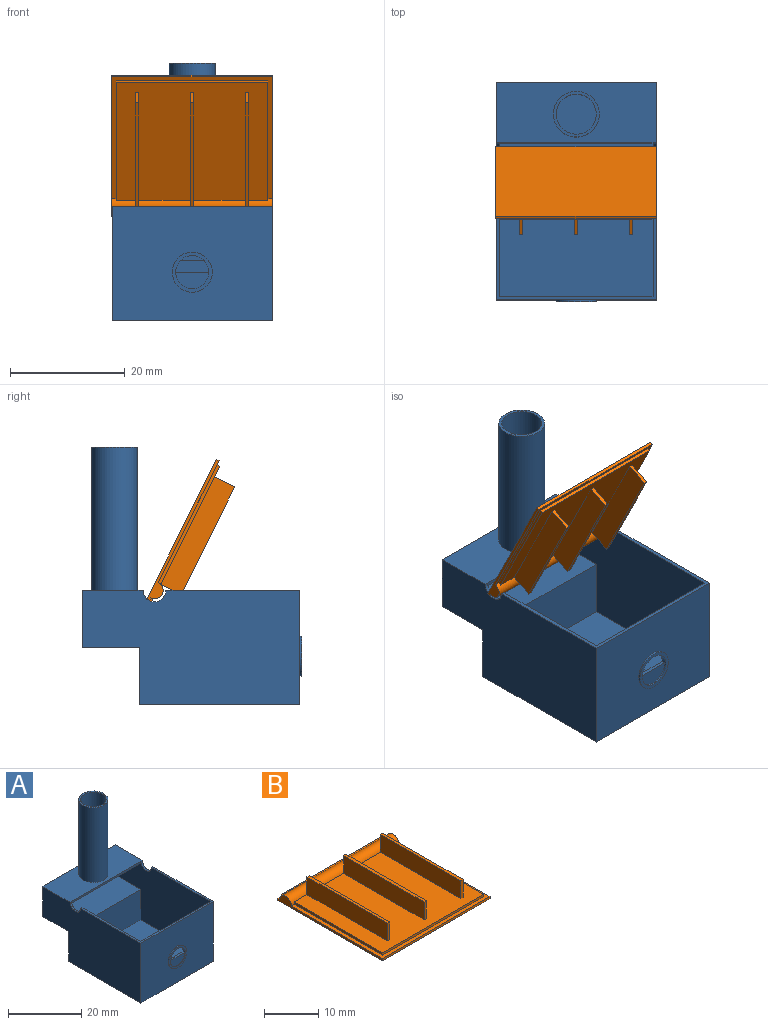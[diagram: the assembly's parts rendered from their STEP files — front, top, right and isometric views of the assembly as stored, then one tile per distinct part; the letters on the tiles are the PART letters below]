
ASSEMBLY  parts=2 mates=1
PART A: 28 faces, bbox 28x38.3x45 mm
  f0: plane 26.8x8.8mm, normal (0,-1,0), area 235.8mm2, adj f3,f5,f14,f27
  f1: plane 38x20mm, normal (-1,0,0), area 653.7mm2, adj f2,f6,f7,f8,f10,f16,f24,f25
  f2: plane 28x28mm, normal (0,0,-1), area 784mm2, adj f1,f4,f7,f25
  f3: plane 36.8x19.5mm, normal (1,0,0), area 604.3mm2, adj f0,f6,f9,f11,f12,f14,f16,f26
  f4: plane 38x20mm, normal (1,0,0), area 653.7mm2, adj f2,f6,f7,f8,f10,f15,f24,f25
  f5: plane 36.8x19.5mm, normal (-1,0,0), area 604.3mm2, adj f0,f6,f9,f11,f12,f14,f15,f26
  f6: plane 28x23.4mm, normal (0,0,1), area 44.2mm2, adj f1,f3,f4,f5,f7,f9,f15,f16
  f7: plane 28x20mm, normal (0,-1,0), area 521.5mm2, adj f1,f2,f4,f6,f18
  f8: plane 28x10mm, normal (0,1,0), area 280mm2, adj f1,f4,f10,f24
  f9: plane 26.8x19.5mm, normal (0,1,0), area 509.4mm2, adj f3,f5,f6,f11,f17,f21
  f10: plane 28x10.6mm, normal (0,0,1), area 246.5mm2, adj f1,f4,f8,f12,f15,f16,f22
  f11: plane 26.8x26.8mm, normal (0,0,1), area 718.2mm2, adj f3,f5,f9,f26
  f12: plane 26.8x0.6mm, normal (0,-1,0), area 16.1mm2, adj f3,f5,f10,f14
  f13: cylinder r=3.5mm len=25.6mm, axis (0,0,1), area 563mm2, adj f14,f23
  f14: plane 26.8x10mm, normal (0,0,-1), area 229.5mm2, adj f0,f3,f5,f12,f13
  f15: cylinder r=2mm len=4mm, axis (-1,0,0), area 3.8mm2, adj f4,f5,f6,f10
  f16: cylinder r=2mm len=4mm, axis (-1,0,0), area 3.8mm2, adj f1,f3,f6,f10
  f17: cylinder r=2.9mm len=5.8mm, axis (0,1,0), area 10.9mm2, adj f9,f19,f20,f21
  f18: cylinder r=3.5mm len=7mm, axis (0,1,0), area 6.6mm2, adj f7,f19
  f19: plane 7x7mm, normal (0,-1,0), area 12.1mm2, adj f17,f18
  f20: plane 5.8x2.9mm, normal (0,-1,0), area 13.2mm2, adj f17,f21
  f21: plane 5.8x0.6mm, normal (0,0,1), area 3.5mm2, adj f9,f17,f20
  f22: cylinder r=4mm len=25mm, axis (0,0,-1), area 628.3mm2, adj f10,f23
  f23: plane 8x8mm, normal (0,0,1), area 11.8mm2, adj f13,f22
  f24: plane 28x10mm, normal (0,0,-1), area 280mm2, adj f1,f4,f8,f25
  f25: plane 28x10mm, normal (0,1,0), area 280mm2, adj f1,f2,f4,f24
  f26: plane 26.8x10.1mm, normal (0,-1,0), area 270.7mm2, adj f3,f5,f11,f27
  f27: plane 26.8x10mm, normal (0,0,1), area 268mm2, adj f0,f3,f5,f26
PART B: 31 faces, bbox 28.1x27.3x5 mm
  f0: plane 26.5x23.09mm, normal (0,0,1), area 574mm2, adj f3,f12,f13,f15,f17,f18,f19,f22
  f1: plane 0.8x0.5mm, normal (0,0,1), area 0.4mm2, adj f6,f7,f11,f15
  f2: plane 0.8x0.5mm, normal (0,0,1), area 0.4mm2, adj f4,f5,f6,f15
  f3: plane 23.09x0.5mm, normal (-1,0,0), area 11.5mm2, adj f0,f9,f12,f15
  f4: plane 0.59x0.5mm, normal (1,0,0), area 0.3mm2, adj f2,f6,f14,f15
  f5: plane 27.3x2mm, normal (1,0,0), area 17.2mm2, adj f2,f6,f8,f9,f10,f15
  f6: plane 28.1x1mm, normal (0,1,0), area 27.3mm2, adj f1,f2,f4,f5,f7,f10,f11,f14
  f7: plane 27.3x2mm, normal (-1,0,0), area 17.2mm2, adj f1,f6,f8,f9,f10,f15
  f8: plane 28.1x0.5mm, normal (0,-1,0), area 14.1mm2, adj f5,f7,f9,f10
  f9: plane 28.1x23.8mm, normal (0,0,1), area 59.3mm2, adj f3,f5,f7,f8,f12,f13,f15
  f10: plane 28.1x27.3mm, normal (0,0,-1), area 767.1mm2, adj f5,f6,f7,f8
  f11: plane 0.59x0.5mm, normal (-1,0,0), area 0.3mm2, adj f1,f6,f14,f15
  f12: plane 26.5x0.5mm, normal (0,-1,0), area 13.3mm2, adj f0,f3,f9,f13
  f13: plane 23.09x0.5mm, normal (1,0,0), area 11.5mm2, adj f0,f9,f12,f15
  f14: plane 26.5x0.59mm, normal (0,0,1), area 15.5mm2, adj f4,f6,f11,f15
  f15: cylinder r=1.5mm len=28.1mm, axis (1,0,0), area 105.4mm2, adj f0,f1,f2,f3,f4,f5,f7,f9
  f16: plane 4x0.6mm, normal (0,1,0), area 2.4mm2, adj f15,f17,f19,f20
  f17: plane 21x4mm, normal (-1,0,0), area 84mm2, adj f0,f16,f18,f20
  f18: plane 4x0.6mm, normal (0,-1,0), area 2.4mm2, adj f0,f17,f19,f20
  f19: plane 21x4mm, normal (1,0,0), area 84mm2, adj f0,f16,f18,f20
  f20: plane 21x0.6mm, normal (0,0,1), area 12.6mm2, adj f16,f17,f18,f19
  f21: plane 4x0.6mm, normal (0,1,0), area 2.4mm2, adj f15,f22,f24,f25
  f22: plane 21x4mm, normal (-1,0,0), area 84mm2, adj f0,f21,f23,f25
  f23: plane 4x0.6mm, normal (0,-1,0), area 2.4mm2, adj f0,f22,f24,f25
  f24: plane 21x4mm, normal (1,0,0), area 84mm2, adj f0,f21,f23,f25
  f25: plane 21x0.6mm, normal (0,0,1), area 12.6mm2, adj f21,f22,f23,f24
  f26: plane 4x0.6mm, normal (0,1,0), area 2.4mm2, adj f15,f27,f29,f30
  f27: plane 21x4mm, normal (-1,0,0), area 84mm2, adj f0,f26,f28,f30
  f28: plane 4x0.6mm, normal (0,-1,0), area 2.4mm2, adj f0,f27,f29,f30
  f29: plane 21x4mm, normal (1,0,0), area 84mm2, adj f0,f26,f28,f30
  f30: plane 21x0.6mm, normal (0,0,1), area 12.6mm2, adj f26,f27,f28,f29
PLACE A t=(-71.28,-12.56,35.21)mm fixed
PLACE B rot(axis=(0,-0.85,0.53),180deg) t=(-57.08,2.37,77.36)mm
MATE revolute A.f15 <-> B.f15  axis (1,0,0) through (-71.28,12.84,55.21)mm
